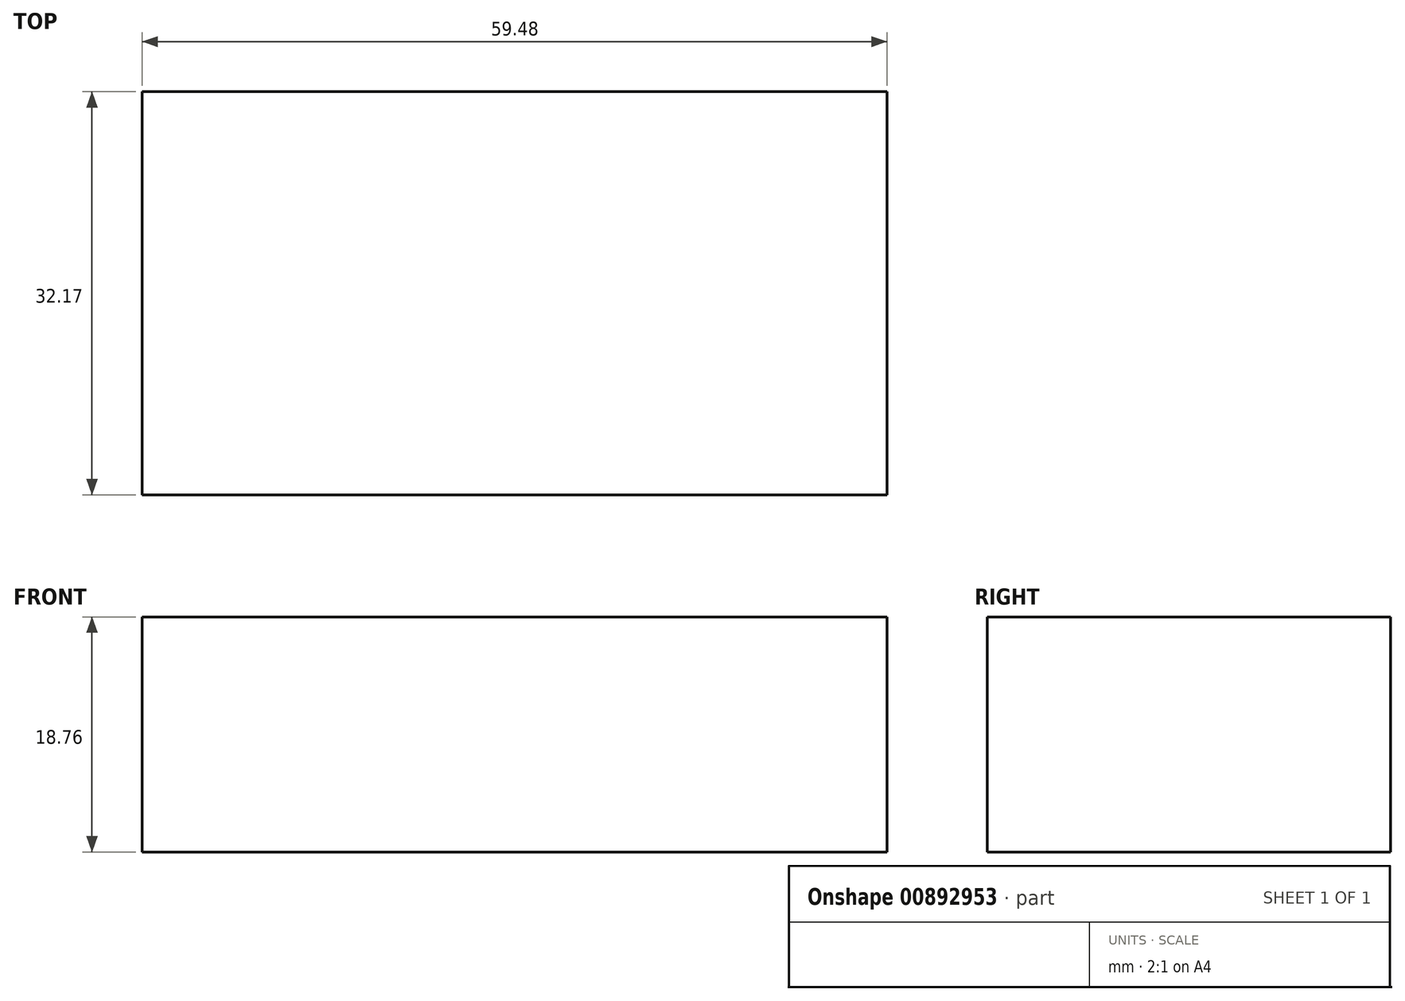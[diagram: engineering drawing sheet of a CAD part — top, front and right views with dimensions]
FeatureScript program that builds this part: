
annotation { "Feature Type Name" : "Feature", "Feature Type Description" : "" }
export const myFeature = defineFeature(function(context is Context, id is Id, definition is map)
    precondition{}
    {
        {
            var Q0;
            Q0=qCreatedBy(makeId("Front.planeOp"),FACE);
            var sketch = newSketch(context, id + "F0", { "sketchPlane" : qUnion([Q0])});
            skLineSegment(sketch, "E0.bottom", {"start": v(-23.66, 9.11) * mm, "end": v(35.82, 9.11) * mm});
            skLineSegment(sketch, "E0.top", {"start": v(-23.66, -9.65) * mm, "end": v(35.82, -9.65) * mm});
            skLineSegment(sketch, "E0.left", {"start": v(-23.66, 9.11) * mm, "end": v(-23.66, -9.65) * mm});
            skLineSegment(sketch, "E0.right", {"start": v(35.82, 9.11) * mm, "end": v(35.82, -9.65) * mm});
            skSolve(sketch);
        }
        {
            var Q0;
            Q0=makeQuery(id+"F0.imprint","IMPRINT",FACE,{"disambiguationData":[TD([[makeQuery(id+"F0.imprint","IMPRINT",EDGE,{"derivedFrom":sQuery(id+"F0.wireOp",EDGE,"E0.bottom")}),-1.0]])]});
            extrude(context, id + "F1", {"entities" : qUnion([Q0]), "depth" : 32.17 * mm, "offsetDistance" : 25.4 * mm});
        }
    });
